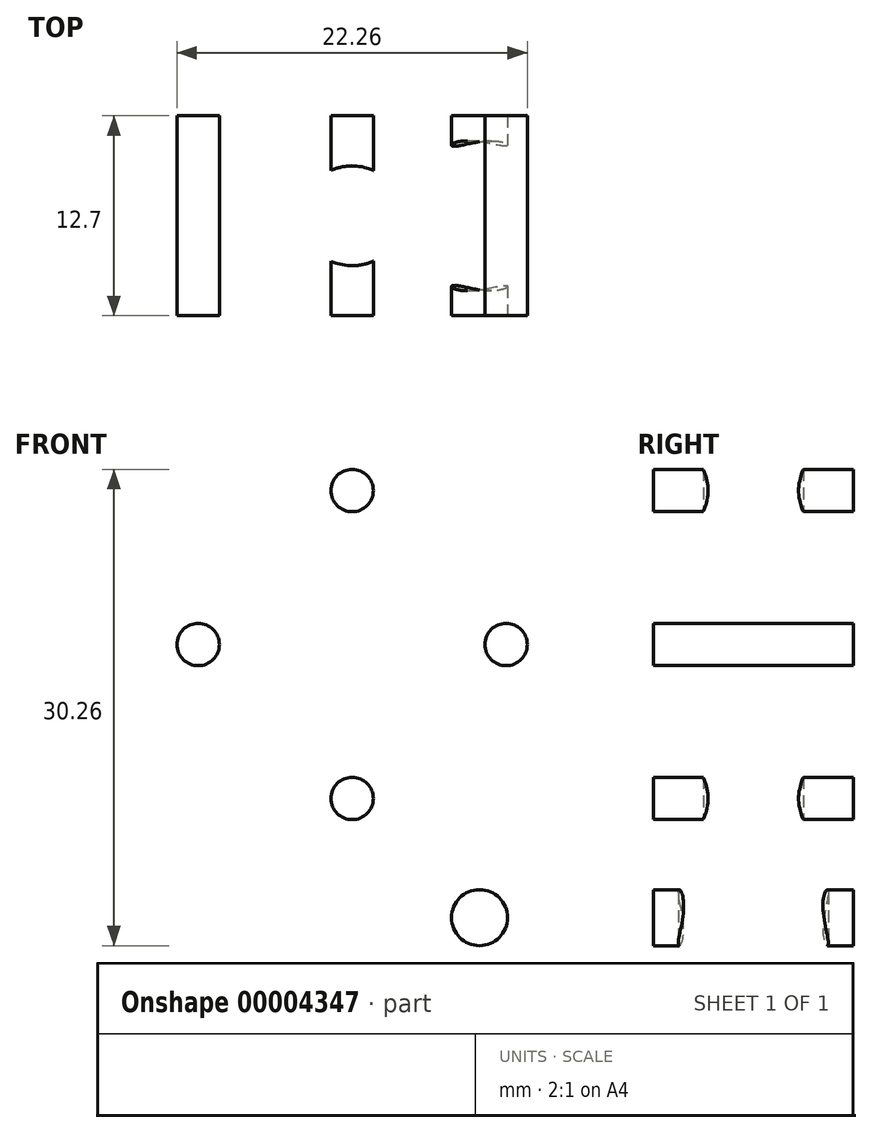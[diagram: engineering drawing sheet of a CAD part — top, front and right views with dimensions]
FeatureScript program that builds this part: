
annotation { "Feature Type Name" : "Feature", "Feature Type Description" : "" }
export const myFeature = defineFeature(function(context is Context, id is Id, definition is map)
    precondition{}
    {
        {
            var Q0;
            Q0=qCreatedBy(makeId("Front.planeOp"),FACE);
            var sketch = newSketch(context, id + "F0", { "sketchPlane" : qUnion([Q0])});
            skCircle(sketch, "E0", {"center": v(0, 0) * mm, "radius": 9.78 * mm, "construction": true});
            skCircle(sketch, "E1", {"center": v(0, 9.78) * mm, "radius": 1.35 * mm});
            skCircle(sketch, "E2.1.0", {"center": v(-6.91, 6.91) * mm, "radius": 1.35 * mm});
            skCircle(sketch, "E2.2.0", {"center": v(-9.78, 0) * mm, "radius": 1.35 * mm});
            skCircle(sketch, "E2.3.0", {"center": v(-6.91, -6.91) * mm, "radius": 1.35 * mm});
            skCircle(sketch, "E2.4.0", {"center": v(0, -9.78) * mm, "radius": 1.35 * mm});
            skCircle(sketch, "E2.5.0", {"center": v(6.91, -6.91) * mm, "radius": 1.35 * mm});
            skCircle(sketch, "E2.6.0", {"center": v(9.78, 0) * mm, "radius": 1.35 * mm});
            skCircle(sketch, "E2.7.0", {"center": v(6.91, 6.91) * mm, "radius": 1.35 * mm});
            skLineSegment(sketch, "E3", {"start": v(-13.46, -28.86) * mm, "end": v(0, 0) * mm, "construction": true});
            skLineSegment(sketch, "E4", {"start": v(0, -31.84) * mm, "end": v(0, 0) * mm, "construction": true});
            skLineSegment(sketch, "E5", {"start": v(0, 0) * mm, "end": v(0, 0) * mm});
            skArc(sketch, "E6", {"start": v(-22.88, -22.15) * mm, "mid": v(-12.43, -29.32) * mm, "end": v(0, -31.84) * mm});
            skArc(sketch, "E7.0.MirrorCS", {"start": v(22.88, -22.15) * mm, "mid": v(12.43, -29.32) * mm, "end": v(0, -31.84) * mm});
            skArc(sketch, "E8", {"start": v(-10.73, -23.02) * mm, "mid": v(-5.5, -24.8) * mm, "end": v(0, -25.4) * mm, "construction": true});
            skLineSegment(sketch, "E9", {"start": v(0, -31.84) * mm, "end": v(0, -31.84) * mm});
            skLineSegment(sketch, "E10", {"start": v(-22.88, -22.15) * mm, "end": v(-11.73, 4.77) * mm});
            skArc(sketch, "E11", {"start": v(-11.73, 4.77) * mm, "mid": v(-7.06, 10.47) * mm, "end": v(0, 12.6) * mm});
            skLineSegment(sketch, "E12.MirrorCS", {"start": v(22.88, -22.15) * mm, "end": v(11.73, 4.77) * mm});
            skArc(sketch, "E13.MirrorCS", {"start": v(11.73, 4.77) * mm, "mid": v(7.06, 10.47) * mm, "end": v(0, 12.6) * mm});
            skSolve(sketch);
        }
        {
            var Q0;
            Q0=makeQuery(id+"F0.imprint","IMPRINT",FACE,{"disambiguationData":[TD([[makeQuery(id+"F0.imprint","IMPRINT",EDGE,{"derivedFrom":sQuery(id+"F0.wireOp",EDGE,"E1")}),1.0]])]});
            var Q1;
            Q1=makeQuery(id+"F0.imprint","IMPRINT",FACE,{"disambiguationData":[TD([[makeQuery(id+"F0.imprint","IMPRINT",EDGE,{"derivedFrom":sQuery(id+"F0.wireOp",EDGE,"E2.6.0")}),1.0]])]});
            var Q2;
            Q2=makeQuery(id+"F0.imprint","IMPRINT",FACE,{"disambiguationData":[TD([[makeQuery(id+"F0.imprint","IMPRINT",EDGE,{"derivedFrom":sQuery(id+"F0.wireOp",EDGE,"E1")}),-1.0]])]});
            var Q3;
            Q3=makeQuery(id+"F0.imprint","IMPRINT",FACE,{"disambiguationData":[TD([[makeQuery(id+"F0.imprint","IMPRINT",EDGE,{"derivedFrom":sQuery(id+"F0.wireOp",EDGE,"E2.4.0")}),1.0]])]});
            var Q4;
            Q4=makeQuery(id+"F0.imprint","IMPRINT",FACE,{"disambiguationData":[TD([[makeQuery(id+"F0.imprint","IMPRINT",EDGE,{"derivedFrom":sQuery(id+"F0.wireOp",EDGE,"E2.2.0")}),1.0]])]});
            extrude(context, id + "F1", {"entities" : qUnion([Q0, Q1, Q2, Q3, Q4]), "oppositeDirection" : true, "depth" : 12.7 * mm});
        }
        {
            var Q0;
            Q0=sQuery(id+"F0.wireOp",EDGE,"E3");
            var Q1;
            Q1=sQuery(id+"F0.wireOp",VERTEX,"E3.start");
            cPlane(context, id + "F2", {"entities" : qUnion([Q0, Q1]), "cplaneType" : CPlaneType.LINE_POINT, "offset" : 152.4 * mm, "width" : 152.4 * mm, "height" : 152.4 * mm});
        }
        {
            var Q0;
            Q0=qCreatedBy(id+"F2.planeOp",FACE);
            var sketch = newSketch(context, id + "F3", { "sketchPlane" : qUnion([Q0])});
            skCircle(sketch, "E14", {"center": v(0, 6.35) * mm, "radius": 4.76 * mm});
            skLineSegment(sketch, "E15", {"start": v(0, 12.7) * mm, "end": v(0, 0) * mm, "construction": true});
            skLineSegment(sketch, "E16", {"start": v(0, 12.7) * mm, "end": v(0, 12.7) * mm});
            skSolve(sketch);
        }
        {
            var Q0;
            Q0=qCreatedBy(makeId("Top.planeOp"),FACE);
            var Q1;
            Q1=sQuery(id+"F0.wireOp",VERTEX,"E6.end");
            cPlane(context, id + "F4", {"entities" : qUnion([Q0, Q1]), "cplaneType" : CPlaneType.PLANE_POINT, "offset" : 152.4 * mm, "width" : 152.4 * mm, "height" : 152.4 * mm});
        }
        {
            var Q0;
            Q0=qCreatedBy(id+"F4.planeOp",FACE);
            var sketch = newSketch(context, id + "F9", { "sketchPlane" : qUnion([Q0])});
            skCircle(sketch, "E17", {"center": v(0, 6.35) * mm, "radius": 3.18 * mm});
            skLineSegment(sketch, "E18", {"start": v(0, 0) * mm, "end": v(0, 12.7) * mm, "construction": true});
            skSolve(sketch);
        }
        {
            var Q0;
            Q0=makeQuery(id+"F3.imprint","IMPRINT",FACE,{"disambiguationData":[TD([[makeQuery(id+"F3.imprint","IMPRINT",EDGE,{"derivedFrom":sQuery(id+"F3.wireOp",EDGE,"E14")}),1.0]])]});
            extrude(context, id + "F5", {"entities" : qUnion([Q0]), "depth" : 19.05 * mm});
        }
        {
            var Q0;
            Q0=makeQuery(id+"F5.opExtrude","SWEPT_BODY",BODY,{"disambiguationData":[OSD([sQuery(id+"F3.wireOp",EDGE,"E14")])]});
            var Q1;
            Q1=qCreatedBy(makeId("Right.planeOp"),FACE);
            mirror(context, id + "F10", {"entities" : qUnion([Q0]), "mirrorPlane" : qUnion([Q1])});
        }
        {
            var Q0;
            Q0=makeQuery(id+"F5.opExtrude","SWEPT_BODY",BODY,{"disambiguationData":[OSD([sQuery(id+"F3.wireOp",EDGE,"E14")])]});
            var Q1;
            Q1=makeQuery(id+"F10.opPattern","COPY",BODY,{"derivedFrom":makeQuery(id+"F5.opExtrude","SWEPT_BODY",BODY,{"disambiguationData":[OSD([sQuery(id+"F3.wireOp",EDGE,"E14")])]}),"instanceName":"1"});
            var Q2;
            Q2=makeQuery(id+"F1.opExtrude","SWEPT_BODY",BODY,{"disambiguationData":[OSD([sQuery(id+"F0.wireOp",EDGE,"E1"),sQuery(id+"F0.wireOp",EDGE,"E2.1.0"),sQuery(id+"F0.wireOp",EDGE,"E2.2.0"),sQuery(id+"F0.wireOp",EDGE,"E2.3.0"),sQuery(id+"F0.wireOp",EDGE,"E2.4.0"),sQuery(id+"F0.wireOp",EDGE,"E2.5.0"),sQuery(id+"F0.wireOp",EDGE,"E2.6.0"),sQuery(id+"F0.wireOp",EDGE,"E2.7.0"),sQuery(id+"F0.wireOp",EDGE,"E7.0.MirrorCS"),sQuery(id+"F0.wireOp",EDGE,"E10"),sQuery(id+"F0.wireOp",EDGE,"E11"),sQuery(id+"F0.wireOp",EDGE,"E6"),sQuery(id+"F0.wireOp",EDGE,"E12.MirrorCS"),sQuery(id+"F0.wireOp",EDGE,"E13.MirrorCS")])]});
            booleanBodies(context, id + "F11", {"operationType" : BooleanOperationType.SUBTRACTION, "tools" : qUnion([Q0, Q1]), "targets" : qUnion([Q2])});
        }
        {
            var Q0;
            Q0=makeQuery(id+"F9.imprint","IMPRINT",FACE,{"disambiguationData":[TD([[makeQuery(id+"F9.imprint","IMPRINT",EDGE,{"derivedFrom":sQuery(id+"F9.wireOp",EDGE,"E17")}),1.0]])]});
            extrude(context, id + "F12", {"entities" : qUnion([Q0]), "operationType" : NewBodyOperationType.REMOVE, "endBound" : BoundingType.THROUGH_ALL, "depth" : 19.05 * mm});
        }
        {
            var Q0;
            Q0=makeQuery(id+"F0.imprint","IMPRINT",FACE,{"disambiguationData":[TD([[makeQuery(id+"F0.imprint","IMPRINT",EDGE,{"derivedFrom":sQuery(id+"F0.wireOp",EDGE,"E1")}),-1.0]])]});
            var sketch = newSketch(context, id + "F6", { "sketchPlane" : qUnion([Q0])});
            skCircle(sketch, "E19", {"center": v(-8.1, -17.35) * mm, "radius": 1.78 * mm});
            skCircle(sketch, "E20", {"center": v(0, -19.14) * mm, "radius": 1.78 * mm});
            skCircle(sketch, "E21.MirrorC", {"center": v(8.1, -17.35) * mm, "radius": 1.78 * mm});
            skSolve(sketch);
        }
        {
            var Q0;
            Q0=makeQuery(id+"F6.imprint","IMPRINT",FACE,{"disambiguationData":[TD([[makeQuery(id+"F6.imprint","IMPRINT",EDGE,{"derivedFrom":sQuery(id+"F6.wireOp",EDGE,"E19")}),1.0]])]});
            var Q1;
            Q1=makeQuery(id+"F6.imprint","IMPRINT",FACE,{"disambiguationData":[TD([[makeQuery(id+"F6.imprint","IMPRINT",EDGE,{"derivedFrom":sQuery(id+"F6.wireOp",EDGE,"E20")}),1.0]])]});
            var Q2;
            Q2=makeQuery(id+"F6.imprint","IMPRINT",FACE,{"disambiguationData":[TD([[makeQuery(id+"F6.imprint","IMPRINT",EDGE,{"derivedFrom":sQuery(id+"F6.wireOp",EDGE,"E21.MirrorC")}),-1.0]])]});
            extrude(context, id + "F7", {"entities" : qUnion([Q0, Q1, Q2]), "operationType" : NewBodyOperationType.REMOVE, "endBound" : BoundingType.UP_TO_NEXT, "oppositeDirection" : true, "depth" : 25.4 * mm});
        }
    });
